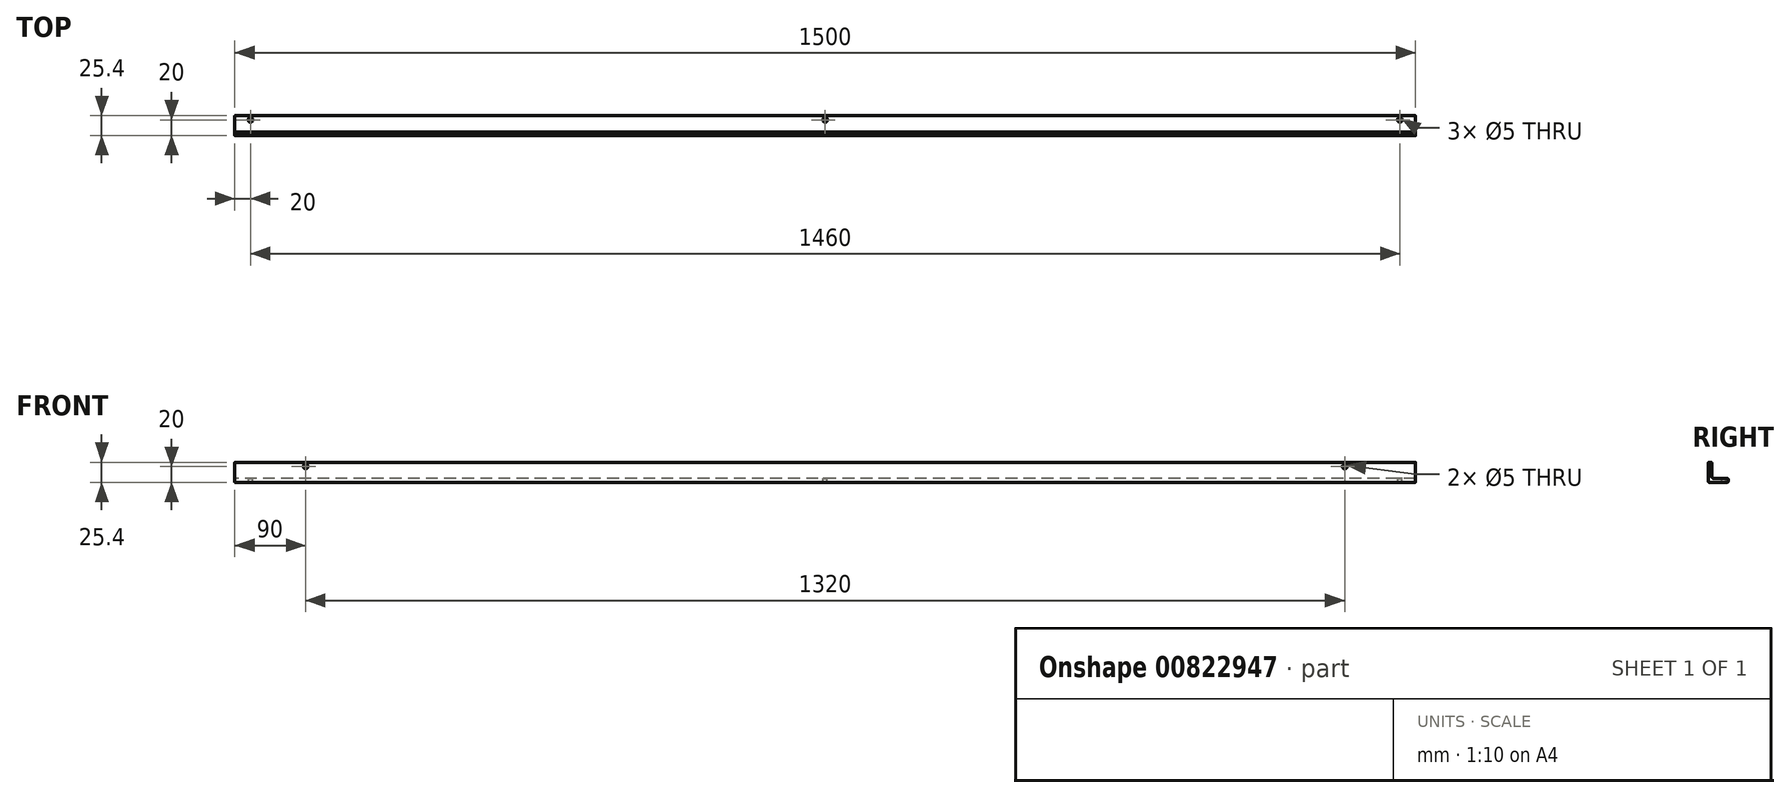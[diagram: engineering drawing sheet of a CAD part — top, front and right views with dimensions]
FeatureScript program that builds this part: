
annotation { "Feature Type Name" : "Feature", "Feature Type Description" : "" }
export const myFeature = defineFeature(function(context is Context, id is Id, definition is map)
    precondition{}
    {
        {
            var Q0;
            Q0=qCreatedBy(makeId("Right.planeOp"),FACE);
            var sketch = newSketch(context, id + "F0", { "sketchPlane" : qUnion([Q0])});
            skLineSegment(sketch, "E0", {"start": v(0, 0) * mm, "end": v(25.4, 0) * mm});
            skLineSegment(sketch, "E1", {"start": v(0, 0) * mm, "end": v(0, 25.4) * mm});
            skLineSegment(sketch, "E2", {"start": v(0, 25.4) * mm, "end": v(4.76, 25.4) * mm});
            skLineSegment(sketch, "E3", {"start": v(4.76, 25.4) * mm, "end": v(4.76, 4.76) * mm});
            skLineSegment(sketch, "E4", {"start": v(4.76, 4.76) * mm, "end": v(25.4, 4.76) * mm});
            skLineSegment(sketch, "E5", {"start": v(25.4, 4.76) * mm, "end": v(25.4, 0) * mm});
            skSolve(sketch);
        }
        {
            var Q0;
            Q0 = qSketchRegion(id + "F0", true);
            extrude(context, id + "F1", {"entities" : qUnion([Q0]), "endBound" : BoundingType.SYMMETRIC, "depth" : 1500 * mm, "offsetDistance" : 25 * mm});
        }
        {
            var Q0;
            Q0=makeQuery(id+"F1.opExtrude","SWEPT_EDGE",EDGE,{"disambiguationData":[OSD([sQuery(id+"F0.wireOp",EDGE,"E1"),sQuery(id+"F0.wireOp",EDGE,"E2")])]});
            var Q1;
            Q1=makeQuery(id+"F1.opExtrude","SWEPT_EDGE",EDGE,{"disambiguationData":[OSD([sQuery(id+"F0.wireOp",EDGE,"E2"),sQuery(id+"F0.wireOp",EDGE,"E3")])]});
            var Q2;
            Q2=makeQuery(id+"F1.opExtrude","SWEPT_EDGE",EDGE,{"disambiguationData":[OSD([sQuery(id+"F0.wireOp",EDGE,"E0"),sQuery(id+"F0.wireOp",EDGE,"E1")])]});
            var Q3;
            Q3=makeQuery(id+"F1.opExtrude","SWEPT_EDGE",EDGE,{"disambiguationData":[OSD([sQuery(id+"F0.wireOp",EDGE,"E4"),sQuery(id+"F0.wireOp",EDGE,"E5")])]});
            var Q4;
            Q4=makeQuery(id+"F1.opExtrude","SWEPT_EDGE",EDGE,{"disambiguationData":[OSD([sQuery(id+"F0.wireOp",EDGE,"E0"),sQuery(id+"F0.wireOp",EDGE,"E5")])]});
            fillet(context, id + "F2", {"entities" : qUnion([Q0, Q1, Q2, Q3, Q4]), "radius" : 1 * mm, "tangentPropagation" : true, "allowEdgeOverflow" : false});
        }
        {
            var Q0;
            Q0=makeQuery(id+"F1.opExtrude","SWEPT_EDGE",EDGE,{"disambiguationData":[OSD([sQuery(id+"F0.wireOp",EDGE,"E3"),sQuery(id+"F0.wireOp",EDGE,"E4")])]});
            fillet(context, id + "F3", {"entities" : qUnion([Q0]), "radius" : (3 * 25.4 / 16 / 2) * mm, "tangentPropagation" : true, "allowEdgeOverflow" : false});
        }
        {
            var Q0;
            Q0=makeQuery(id+"F1.opExtrude","SWEPT_FACE",FACE,{"disambiguationData":[OSD([sQuery(id+"F0.wireOp",EDGE,"E4")])]});
            var sketch = newSketch(context, id + "F4", { "sketchPlane" : qUnion([Q0])});
            skLineSegment(sketch, "E6.0", {"start": v(-750, 0) * mm, "end": v(750, 0) * mm, "construction": true});
            skLineSegment(sketch, "E7.0", {"start": v(-750, 1) * mm, "end": v(-750, 24.4) * mm, "construction": true});
            skCircle(sketch, "E8", {"center": v(-730, 20) * mm, "radius": 2.5 * mm});
            skLineSegment(sketch, "E9.0", {"start": v(-750, 25.4) * mm, "end": v(750, 25.4) * mm, "construction": true});
            skCircle(sketch, "E10.1.0.0", {"center": v(-365, 20) * mm, "radius": 2.5 * mm, "construction": true});
            skCircle(sketch, "E10.2.0.0", {"center": v(0, 20) * mm, "radius": 2.5 * mm});
            skCircle(sketch, "E10.3.0.0", {"center": v(365, 20) * mm, "radius": 2.5 * mm, "construction": true});
            skCircle(sketch, "E10.4.0.0", {"center": v(730, 20) * mm, "radius": 2.5 * mm});
            skLineSegment(sketch, "E10.direction1", {"start": v(-730, 20) * mm, "end": v(-365, 20) * mm, "construction": true});
            skSolve(sketch);
        }
        {
            var Q0;
            Q0 = qSketchRegion(id + "F4", true);
            extrude(context, id + "F5", {"entities" : qUnion([Q0]), "operationType" : NewBodyOperationType.REMOVE, "oppositeDirection" : true, "depth" : 25 * mm, "offsetDistance" : 25 * mm});
        }
        {
            var Q0;
            Q0=makeQuery(id+"F5.boolean.opBoolean","COPY",FACE,{"derivedFrom":makeQuery(id+"F5.opExtrude","SWEPT_FACE",FACE,{"disambiguationData":[OSD([sQuery(id+"F4.wireOp",EDGE,"E8")])]})});
            var Q1;
            Q1=makeQuery(id+"F5.boolean.opBoolean","COPY",FACE,{"derivedFrom":makeQuery(id+"F5.opExtrude","SWEPT_FACE",FACE,{"disambiguationData":[OSD([sQuery(id+"F4.wireOp",EDGE,"E10.1.0.0")])]})});
            var Q2;
            Q2=makeQuery(id+"F5.boolean.opBoolean","COPY",FACE,{"derivedFrom":makeQuery(id+"F5.opExtrude","SWEPT_FACE",FACE,{"disambiguationData":[OSD([sQuery(id+"F4.wireOp",EDGE,"E10.2.0.0")])]})});
            var Q3;
            Q3=makeQuery(id+"F5.boolean.opBoolean","COPY",FACE,{"derivedFrom":makeQuery(id+"F5.opExtrude","SWEPT_FACE",FACE,{"disambiguationData":[OSD([sQuery(id+"F4.wireOp",EDGE,"E10.3.0.0")])]})});
            var Q4;
            Q4=makeQuery(id+"F5.boolean.opBoolean","COPY",FACE,{"derivedFrom":makeQuery(id+"F5.opExtrude","SWEPT_FACE",FACE,{"disambiguationData":[OSD([sQuery(id+"F4.wireOp",EDGE,"E10.4.0.0")])]})});
            chamfer(context, id + "F6", {"entities" : qUnion([Q0, Q1, Q2, Q3, Q4]), "width" : 0.5 * mm, "tangentPropagation" : true});
        }
        {
            var Q0;
            Q0=makeQuery(id+"F1.opExtrude","SWEPT_FACE",FACE,{"disambiguationData":[OSD([sQuery(id+"F0.wireOp",EDGE,"E1")])]});
            var sketch = newSketch(context, id + "F7", { "sketchPlane" : qUnion([Q0])});
            skLineSegment(sketch, "E11.0", {"start": v(-750, 1) * mm, "end": v(-750, 24.4) * mm, "construction": true});
            skLineSegment(sketch, "E12.0", {"start": v(750, 0) * mm, "end": v(-750, 0) * mm, "construction": true});
            skCircle(sketch, "E13", {"center": v(-660, 20) * mm, "radius": 2.5 * mm});
            skLineSegment(sketch, "E14", {"start": v(0, 0) * mm, "end": v(0, -130.93) * mm, "construction": true});
            skCircle(sketch, "E15.MirrorC", {"center": v(660, 20) * mm, "radius": 2.5 * mm});
            skSolve(sketch);
        }
        {
            var Q0;
            Q0 = qSketchRegion(id + "F7", true);
            extrude(context, id + "F8", {"entities" : qUnion([Q0]), "operationType" : NewBodyOperationType.REMOVE, "oppositeDirection" : true, "depth" : 25 * mm, "offsetDistance" : 25 * mm});
        }
        {
            var Q0;
            Q0=makeQuery(id+"F8.boolean.opBoolean","COPY",FACE,{"derivedFrom":makeQuery(id+"F8.opExtrude","SWEPT_FACE",FACE,{"disambiguationData":[OSD([sQuery(id+"F7.wireOp",EDGE,"E13")])]})});
            var Q1;
            Q1=makeQuery(id+"F8.boolean.opBoolean","COPY",FACE,{"derivedFrom":makeQuery(id+"F8.opExtrude","SWEPT_FACE",FACE,{"disambiguationData":[OSD([sQuery(id+"F7.wireOp",EDGE,"E15.MirrorC")])]})});
            chamfer(context, id + "F9", {"entities" : qUnion([Q0, Q1]), "width" : 0.5 * mm, "tangentPropagation" : true});
        }
    });
